# Revit family: QF_HOSHIZAKI_131141070
name_source: partatom
category: Specialty Equipment
revit_build: Autodesk Revit 2016 (Build: 20150220_1215(x64)
units: mm (PartAtom-declared; Revit-internal decimal feet)

## family parameters
Always vertical = Yes
Cut with Voids When Loaded = No
OmniClass Number = 23.40.40.14
OmniClass Title = Food Service Equipment
Part Type = Normal
Room Calculation Point = No
Round Connector Dimension = Use Diameter
Shared = No
Work Plane-Based = No

## types (1)
- 131141070_230V/1Ph/50Hz
    Accessory = No
    Apparent Power = 2540 VA
    Assembly Code = E1090320
    Conn Conduit = No
    Cost = 0 $
    Cycle = 50 Hz
    Depth Actual = 830 mm  [stored 2.7231 ft]
    Description = ADVANCE DOUBLE DOOR REFRIGERATOR, 2/1 GN DEEP, AISI430 STAINLESS STEEL EXTERIOR AND INTERIOR, HC NATURAL REFRIGERANT, LEGS
    Electric power = 2540 W
    FL Amps = 11 A
    Height Actual = 2000 mm
    Length Actual = 1344 mm  [stored 4.40945 ft]
    Manufacturer = HOSHIZAKI
    Max Overcurrent Protection = 0 A
    Min Ckt Ampacity = 0 A
    Model = ADVANCE K 140-4 L
    Number of Poles = 2
    Phase = 1
    URL = www.hoshizaki-europe.com
    Volts = 230 V
    Weight = 183.00 kg

note: [stored X ft] marks values corroborated as IEEE doubles in the binary element streams (Revit-internal decimal feet)

## geometry (parser evidence)
native form markers: Blend x6, Sweep x10
no freeform markers — native parametric forms only
